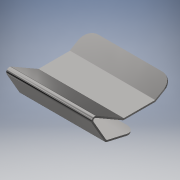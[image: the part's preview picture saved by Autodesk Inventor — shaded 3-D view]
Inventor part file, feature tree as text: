
AUTODESK INVENTOR PART (.ipt)
format: ipt  version: 2018 (Build 220112000, 112)  size: 182,784 bytes
history: native  units: mm
features: other x19, sketch x6, hole x1
ambient origin geometry x8: Origin, YZ Plane, XZ Plane, XY Plane, X Axis, Y Axis, Z Axis, Center Point
bodies: Solido1 (feature_tree)
feature tree (26):
  other  "Faccia1"
  other  "Flangia1"
  other  "Flangia2"
  other  "Flangia3"
  other  "Flangia5"
  hole  "Foro1"  [1 undecoded]
  other  "Arrotondamento angolo1"
  sketch  "Schizzo1"
  other  "Piano1"
  sketch  "Schizzo2"
  other  "Piano2"
  other  "Piega (Bend)1"
  other  "Angolo1"
  sketch  "Schizzo3"
  other  "Piano3"
  other  "Piega (Bend)2"
  other  "Angolo2"
  sketch  "Schizzo4"
  other  "Piano4"
  other  "Piega (Bend)3"
  other  "Angolo3"
  sketch  "Schizzo6"
  other  "Piano6"
  other  "Piega (Bend)5"
  other  "Angolo5"
  sketch  "Schizzo7"
note: 1 required parameter value undecoded (feature->parameter linkage not recoverable at this tier; creation-order binding heuristic only, values carry confidence <= 0.55)
